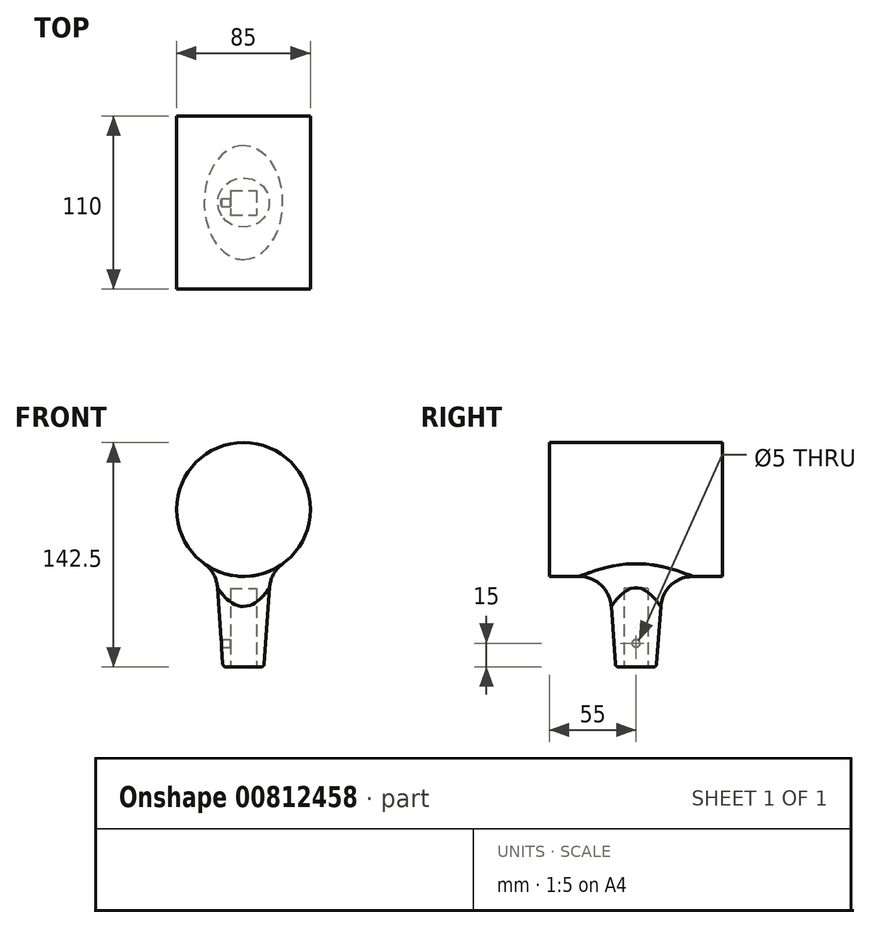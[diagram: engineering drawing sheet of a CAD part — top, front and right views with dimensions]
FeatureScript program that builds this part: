
annotation { "Feature Type Name" : "Feature", "Feature Type Description" : "" }
export const myFeature = defineFeature(function(context is Context, id is Id, definition is map)
    precondition{}
    {
        {
            var Q0;
            Q0=qCreatedBy(makeId("Front.planeOp"),FACE);
            var sketch = newSketch(context, id + "F0", { "sketchPlane" : qUnion([Q0])});
            skCircle(sketch, "E0", {"center": v(0, 0) * mm, "radius": 42.5 * mm});
            skSolve(sketch);
        }
        {
            var Q0;
            Q0=makeQuery(id+"F0.imprint","IMPRINT",FACE,{"disambiguationData":[TD([[makeQuery(id+"F0.imprint","IMPRINT",EDGE,{"derivedFrom":sQuery(id+"F0.wireOp",EDGE,"E0")}),1.0]])]});
            extrude(context, id + "F1", {"entities" : qUnion([Q0]), "endBound" : BoundingType.SYMMETRIC, "depth" : 110 * mm, "offsetDistance" : 25 * mm});
        }
        {
            var Q0;
            Q0=qCreatedBy(makeId("Top.planeOp"),FACE);
            var sketch = newSketch(context, id + "F2", { "sketchPlane" : qUnion([Q0])});
            skCircle(sketch, "E1", {"center": v(0, 0) * mm, "radius": 20 * mm});
            skSolve(sketch);
        }
        {
            var Q0;
            Q0=qSketchRegion(id+"F2",true);
            extrude(context, id + "F3", {"entities" : qUnion([Q0]), "operationType" : NewBodyOperationType.ADD, "oppositeDirection" : true, "depth" : 100 * mm, "offsetDistance" : 25 * mm, "hasDraft" : true, "draftAngle" : 4 * degree, "draftPullDirection" : true});
        }
        {
            var Q0;
            Q0=makeQuery(id+"F3.opExtrude","CAP_FACE",FACE,{"disambiguationData":[OSD([sQuery(id+"F2.wireOp",EDGE,"E1")])],"isStart":false});
            var sketch = newSketch(context, id + "F4", { "sketchPlane" : qUnion([Q0])});
            skLineSegment(sketch, "E2.bottom", {"start": v(-8.26, -7.6) * mm, "end": v(8.15, -7.6) * mm});
            skLineSegment(sketch, "E2.top", {"start": v(-8.26, 7.8) * mm, "end": v(8.15, 7.8) * mm});
            skLineSegment(sketch, "E2.left", {"start": v(-8.26, -7.6) * mm, "end": v(-8.26, 7.8) * mm});
            skLineSegment(sketch, "E2.right", {"start": v(8.15, -7.6) * mm, "end": v(8.15, 7.8) * mm});
            skSolve(sketch);
        }
        {
            var Q0;
            Q0=qSketchRegion(id+"F4",true);
            extrude(context, id + "F5", {"entities" : qUnion([Q0]), "operationType" : NewBodyOperationType.REMOVE, "oppositeDirection" : true, "depth" : 50 * mm, "offsetDistance" : 25 * mm});
        }
        {
            var Q0;
            Q0=qCreatedBy(makeId("Right.planeOp"),FACE);
            var sketch = newSketch(context, id + "F6", { "sketchPlane" : qUnion([Q0])});
            skCircle(sketch, "E3", {"center": v(0, -85) * mm, "radius": 2.5 * mm});
            skSolve(sketch);
        }
        {
            var Q0;
            Q0=qSketchRegion(id+"F6",true);
            extrude(context, id + "F7", {"entities" : qUnion([Q0]), "operationType" : NewBodyOperationType.REMOVE, "oppositeDirection" : true, "depth" : 50 * mm, "offsetDistance" : 25 * mm});
        }
        {
            var Q0;
            Q0=makeQuery(id+"F3.boolean.opBoolean","INTERSECT",EDGE,{"derivedFrom":[makeQuery(id+"F1.opExtrude","SWEPT_FACE",FACE,{"disambiguationData":[OSD([sQuery(id+"F0.wireOp",EDGE,"E0")])]}),makeQuery(id+"F3.opExtrude","SWEPT_FACE",FACE,{"disambiguationData":[OSD([sQuery(id+"F2.wireOp",EDGE,"E1")])]})]});
            fillet(context, id + "F8", {"entities" : qUnion([Q0]), "radius" : 20.5 * mm, "tangentPropagation" : true, "allowEdgeOverflow" : false});
        }
        {
            var Q0;
            Q0=makeQuery(id+"F3.opExtrude","CAP_EDGE",EDGE,{"disambiguationData":[OSD([sQuery(id+"F2.wireOp",EDGE,"E1")])],"isStart":false});
            fillet(context, id + "F9", {"entities" : qUnion([Q0]), "radius" : 2 * mm, "tangentPropagation" : true, "allowEdgeOverflow" : false});
        }
    });
